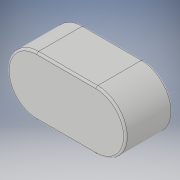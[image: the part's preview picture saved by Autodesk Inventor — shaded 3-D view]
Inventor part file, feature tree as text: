
AUTODESK INVENTOR PART (.ipt)
format: ipt  version: 2019.4 (Build 234330000, 330)  size: 119,808 bytes
history: native  units: mm
features: other x1, extrude x1, fillet x1, sketch x1
ambient origin geometry x8: Origin, YZ Plane, XZ Plane, XY Plane, X Axis, Y Axis, Z Axis, Center Point
bodies: Body1 (feature_tree)
feature tree (4):
  other  "實體1"
  extrude  "擠出1"  Depth=5.0mm
  fillet  "圓角1"  Radius=5.0mm
  sketch  "草圖1"
